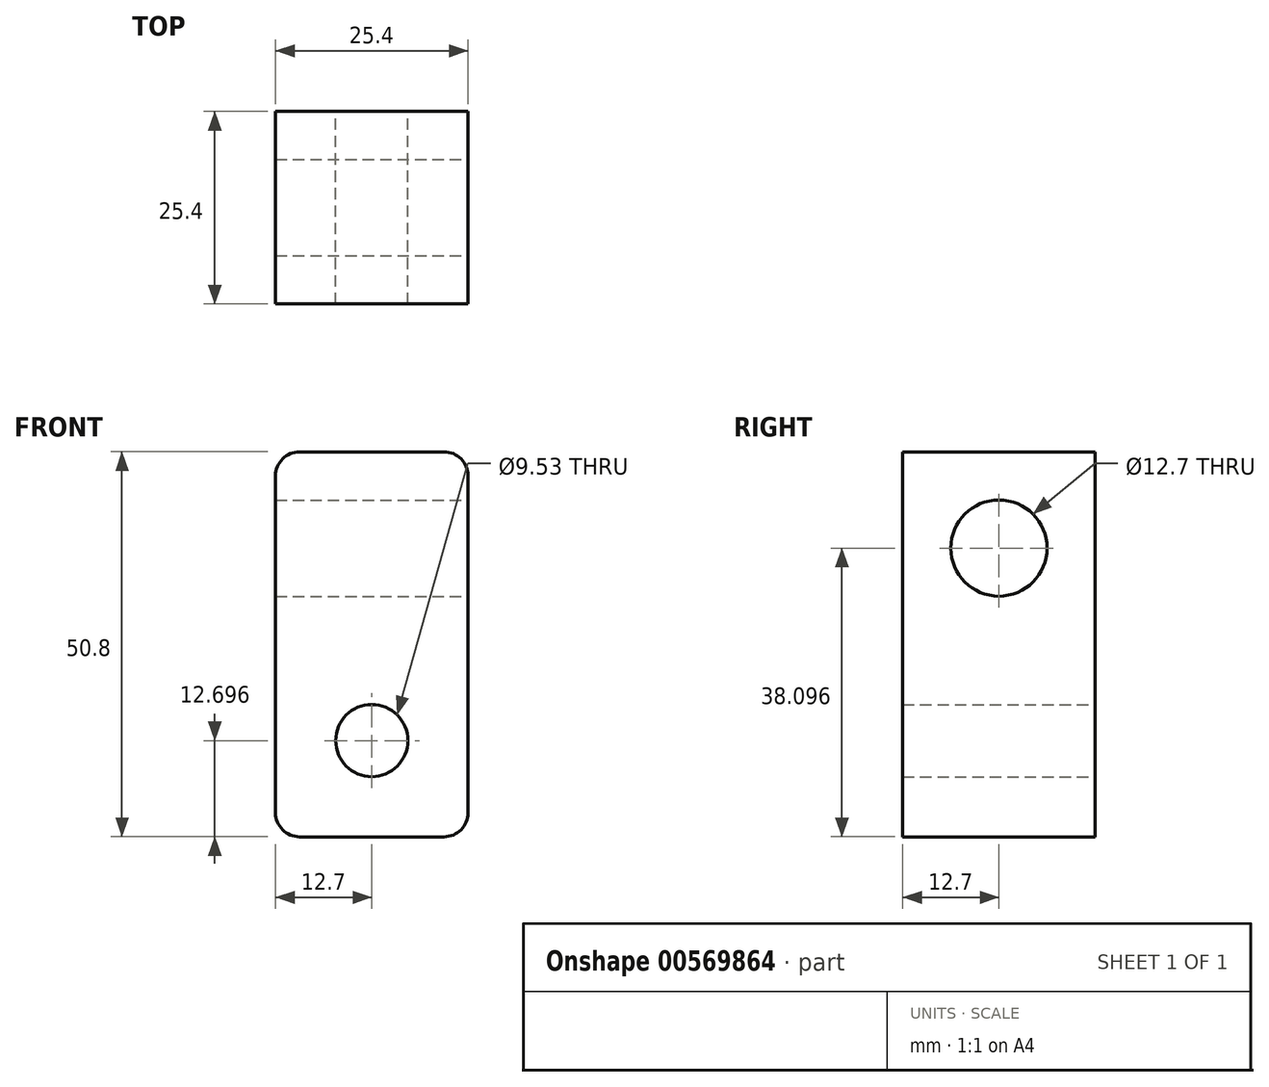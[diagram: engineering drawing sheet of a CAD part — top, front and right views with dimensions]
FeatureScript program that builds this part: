
annotation { "Feature Type Name" : "Feature", "Feature Type Description" : "" }
export const myFeature = defineFeature(function(context is Context, id is Id, definition is map)
    precondition{}
    {
        {
            var Q0;
            Q0=qCreatedBy(makeId("Front.planeOp"),FACE);
            var sketch = newSketch(context, id + "F0", { "sketchPlane" : qUnion([Q0])});
            skLineSegment(sketch, "E0.bottom", {"start": v(-17.58, -29.56) * mm, "end": v(1.47, -29.56) * mm});
            skLineSegment(sketch, "E0.top", {"start": v(-17.58, 21.24) * mm, "end": v(1.47, 21.24) * mm});
            skLineSegment(sketch, "E0.left", {"start": v(-20.75, -26.39) * mm, "end": v(-20.75, 18.06) * mm});
            skLineSegment(sketch, "E0.right", {"start": v(4.65, -26.39) * mm, "end": v(4.65, 18.06) * mm});
            skPoint(sketch, "E1.visualSharp", {"position": v(-20.75, 21.24) * mm});
            skArc(sketch, "E1.filletArc", {"start": v(-17.58, 21.24) * mm, "mid": v(-19.82, 20.3) * mm, "end": v(-20.75, 18.06) * mm});
            skPoint(sketch, "E2.visualSharp", {"position": v(4.65, 21.24) * mm});
            skArc(sketch, "E2.filletArc", {"start": v(4.65, 18.06) * mm, "mid": v(3.72, 20.3) * mm, "end": v(1.47, 21.24) * mm});
            skPoint(sketch, "E3.visualSharp", {"position": v(-20.75, -29.56) * mm});
            skArc(sketch, "E3.filletArc", {"start": v(-20.75, -26.39) * mm, "mid": v(-19.82, -28.63) * mm, "end": v(-17.58, -29.56) * mm});
            skPoint(sketch, "E4.visualSharp", {"position": v(4.65, -29.56) * mm});
            skArc(sketch, "E4.filletArc", {"start": v(1.47, -29.56) * mm, "mid": v(3.72, -28.63) * mm, "end": v(4.65, -26.39) * mm});
            skSolve(sketch);
        }
        {
            var Q0;
            Q0 = qSketchRegion(id + "F0", true);
            extrude(context, id + "F1", {"entities" : qUnion([Q0]), "depth" : 25.4 * mm, "offsetDistance" : 25.4 * mm});
        }
        {
            var Q0;
            Q0=makeQuery(id+"F1.opExtrude","SWEPT_FACE",FACE,{"disambiguationData":[OSD([sQuery(id+"F0.wireOp",EDGE,"E0.right")])]});
            var sketch = newSketch(context, id + "F2", { "sketchPlane" : qUnion([Q0])});
            skCircle(sketch, "E5", {"center": v(-12.7, 8.54) * mm, "radius": 6.35 * mm});
            skSolve(sketch);
        }
        {
            var Q0;
            Q0 = qSketchRegion(id + "F2", true);
            extrude(context, id + "F3", {"entities" : qUnion([Q0]), "operationType" : NewBodyOperationType.REMOVE, "oppositeDirection" : true, "depth" : 25.4 * mm, "offsetDistance" : 25.4 * mm});
        }
        {
            var Q0;
            Q0=makeQuery(id+"F1.opExtrude","CAP_FACE",FACE,{"disambiguationData":[OSD([sQuery(id+"F0.wireOp",EDGE,"E0.bottom"),sQuery(id+"F0.wireOp",EDGE,"E0.top"),sQuery(id+"F0.wireOp",EDGE,"E0.left"),sQuery(id+"F0.wireOp",EDGE,"E0.right"),sQuery(id+"F0.wireOp",EDGE,"E1.filletArc"),sQuery(id+"F0.wireOp",EDGE,"E2.filletArc"),sQuery(id+"F0.wireOp",EDGE,"E3.filletArc"),sQuery(id+"F0.wireOp",EDGE,"E4.filletArc")])],"isStart":true});
            var sketch = newSketch(context, id + "F4", { "sketchPlane" : qUnion([Q0])});
            skCircle(sketch, "E6", {"center": v(8.05, -16.86) * mm, "radius": 4.76 * mm});
            skSolve(sketch);
        }
        {
            var Q0;
            Q0 = qSketchRegion(id + "F4", true);
            extrude(context, id + "F5", {"entities" : qUnion([Q0]), "operationType" : NewBodyOperationType.REMOVE, "oppositeDirection" : true, "depth" : 25.4 * mm, "offsetDistance" : 25.4 * mm});
        }
    });
